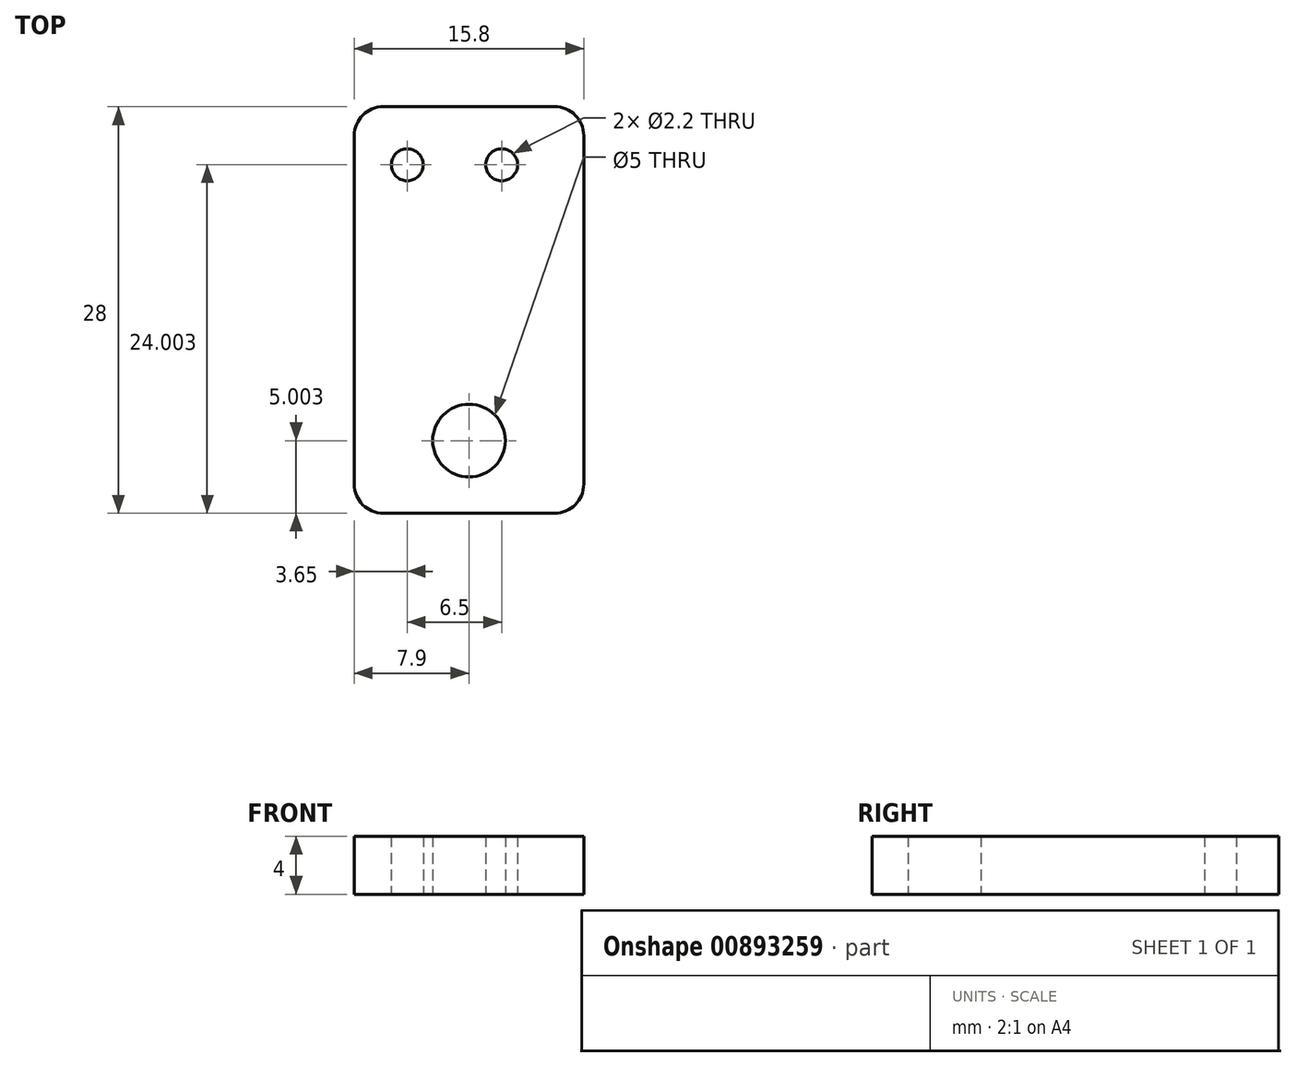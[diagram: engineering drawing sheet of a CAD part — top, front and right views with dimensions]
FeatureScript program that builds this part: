
annotation { "Feature Type Name" : "Feature", "Feature Type Description" : "" }
export const myFeature = defineFeature(function(context is Context, id is Id, definition is map)
    precondition{}
    {
        {
            var Q0;
            Q0=qCreatedBy(makeId("Top.planeOp"),FACE);
            var sketch = newSketch(context, id + "F0", { "sketchPlane" : qUnion([Q0])});
            skLineSegment(sketch, "E0.bottom", {"start": v(0, 23.83) * mm, "end": v(0, 23.83) * mm});
            skLineSegment(sketch, "E0.top", {"start": v(0, -23.13) * mm, "end": v(0, -23.13) * mm});
            skLineSegment(sketch, "E0.left", {"start": v(0, 23.83) * mm, "end": v(0, -23.13) * mm, "construction": true});
            skLineSegment(sketch, "E0.right", {"start": v(0, 23.83) * mm, "end": v(0, -23.13) * mm, "construction": true});
            skLineSegment(sketch, "E1", {"start": v(0, 16.4) * mm, "end": v(-7.9, 16.4) * mm});
            skLineSegment(sketch, "E2", {"start": v(-7.9, 16.4) * mm, "end": v(-7.9, -11.6) * mm});
            skLineSegment(sketch, "E3", {"start": v(-7.9, -11.6) * mm, "end": v(0, -11.6) * mm});
            skLineSegment(sketch, "E4.MirrorCS", {"start": v(0, 16.4) * mm, "end": v(7.9, 16.4) * mm});
            skLineSegment(sketch, "E5.MirrorCS", {"start": v(7.9, 16.4) * mm, "end": v(7.9, -11.6) * mm});
            skLineSegment(sketch, "E6.MirrorCS", {"start": v(7.9, -11.6) * mm, "end": v(0, -11.6) * mm});
            skCircle(sketch, "E7", {"center": v(0, -6.6) * mm, "radius": 2.5 * mm});
            skCircle(sketch, "E8", {"center": v(-4.25, 12.4) * mm, "radius": 1.1 * mm});
            skCircle(sketch, "E9.MirrorC", {"center": v(2.25, 12.4) * mm, "radius": 1.1 * mm});
            skSolve(sketch);
        }
        {
            var Q0;
            Q0=makeQuery(id+"F0.imprint","IMPRINT",FACE,{"disambiguationData":[TD([[makeQuery(id+"F0.imprint","IMPRINT",EDGE,{"derivedFrom":sQuery(id+"F0.wireOp",EDGE,"E1")}),1.0]])]});
            extrude(context, id + "F1", {"entities" : qUnion([Q0]), "offsetDistance" : 25 * mm, "depth" : 4 * mm});
        }
        {
            var Q0;
            Q0=makeQuery(id+"F1.opExtrude","SWEPT_EDGE",EDGE,{"disambiguationData":[OSD([sQuery(id+"F0.wireOp",EDGE,"E5.MirrorCS"),sQuery(id+"F0.wireOp",EDGE,"E6.MirrorCS")])]});
            var Q1;
            Q1=makeQuery(id+"F1.opExtrude","SWEPT_EDGE",EDGE,{"disambiguationData":[OSD([sQuery(id+"F0.wireOp",EDGE,"E4.MirrorCS"),sQuery(id+"F0.wireOp",EDGE,"E5.MirrorCS")])]});
            var Q2;
            Q2=makeQuery(id+"F1.opExtrude","SWEPT_EDGE",EDGE,{"disambiguationData":[OSD([sQuery(id+"F0.wireOp",EDGE,"E2"),sQuery(id+"F0.wireOp",EDGE,"E3")])]});
            var Q3;
            Q3=makeQuery(id+"F1.opExtrude","SWEPT_EDGE",EDGE,{"disambiguationData":[OSD([sQuery(id+"F0.wireOp",EDGE,"E1"),sQuery(id+"F0.wireOp",EDGE,"E2")])]});
            fillet(context, id + "F2", {"entities" : qUnion([Q0, Q1, Q2, Q3]), "radius" : 2 * mm, "tangentPropagation" : true, "allowEdgeOverflow" : false});
        }
    });
